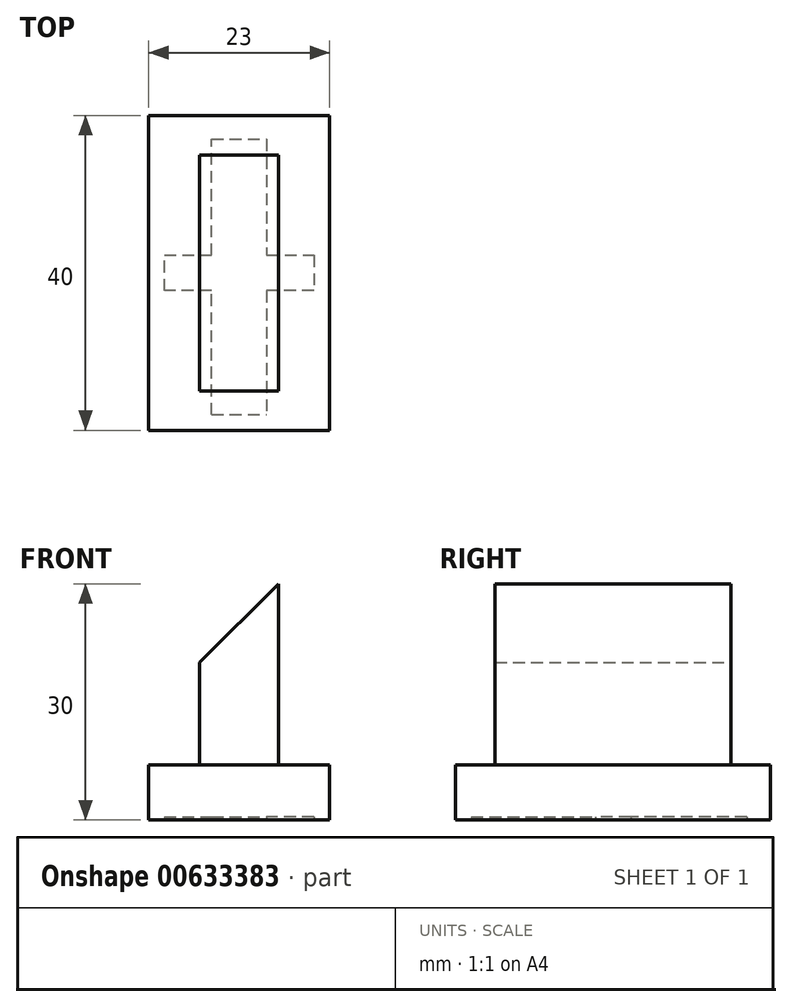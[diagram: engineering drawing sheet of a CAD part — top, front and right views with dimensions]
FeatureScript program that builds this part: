
annotation { "Feature Type Name" : "Feature", "Feature Type Description" : "" }
export const myFeature = defineFeature(function(context is Context, id is Id, definition is map)
    precondition{}
    {
        {
            var Q0;
            Q0=qCreatedBy(makeId("Top.planeOp"),FACE);
            var sketch = newSketch(context, id + "F0", { "sketchPlane" : qUnion([Q0])});
            skLineSegment(sketch, "E0.bottom", {"start": v(0, 0) * mm, "end": v(23, 0) * mm});
            skLineSegment(sketch, "E0.top", {"start": v(0, 40) * mm, "end": v(23, 40) * mm});
            skLineSegment(sketch, "E0.left", {"start": v(0, 0) * mm, "end": v(0, 40) * mm});
            skLineSegment(sketch, "E0.right", {"start": v(23, 0) * mm, "end": v(23, 40) * mm});
            skSolve(sketch);
        }
        {
            var Q0;
            Q0 = qSketchRegion(id + "F0", true);
            extrude(context, id + "F1", {"entities" : qUnion([Q0]), "depth" : 7 * mm, "offsetDistance" : 25 * mm});
        }
        {
            var Q0;
            Q0=qCreatedBy(makeId("Top.planeOp"),FACE);
            var sketch = newSketch(context, id + "F2", { "sketchPlane" : qUnion([Q0])});
            skLineSegment(sketch, "E1.bottom", {"start": v(6.5, 35) * mm, "end": v(16.5, 35) * mm});
            skLineSegment(sketch, "E1.top", {"start": v(6.5, 5) * mm, "end": v(16.5, 5) * mm});
            skLineSegment(sketch, "E1.left", {"start": v(6.5, 35) * mm, "end": v(6.5, 5) * mm});
            skLineSegment(sketch, "E1.right", {"start": v(16.5, 35) * mm, "end": v(16.5, 5) * mm});
            skSolve(sketch);
        }
        {
            var Q0;
            Q0 = qSketchRegion(id + "F2", true);
            extrude(context, id + "F3", {"entities" : qUnion([Q0]), "operationType" : NewBodyOperationType.ADD, "depth" : 30 * mm, "offsetDistance" : 25 * mm});
        }
        {
            var Q0;
            Q0=qCreatedBy(makeId("Top.planeOp"),FACE);
            var sketch = newSketch(context, id + "F4", { "sketchPlane" : qUnion([Q0])});
            skLineSegment(sketch, "E2", {"start": v(8, 2) * mm, "end": v(8, 17.75) * mm});
            skLineSegment(sketch, "E3", {"start": v(8, 17.75) * mm, "end": v(2, 17.75) * mm});
            skLineSegment(sketch, "E4", {"start": v(2, 17.75) * mm, "end": v(2, 22.25) * mm});
            skLineSegment(sketch, "E5", {"start": v(2, 22.25) * mm, "end": v(8, 22.25) * mm});
            skLineSegment(sketch, "E6", {"start": v(8, 22.25) * mm, "end": v(8, 37) * mm});
            skLineSegment(sketch, "E7", {"start": v(8, 37) * mm, "end": v(15, 37) * mm});
            skLineSegment(sketch, "E8", {"start": v(15, 37) * mm, "end": v(15, 22.25) * mm});
            skLineSegment(sketch, "E9", {"start": v(15, 22.25) * mm, "end": v(21, 22.25) * mm});
            skLineSegment(sketch, "E10", {"start": v(21, 22.25) * mm, "end": v(21, 17.75) * mm});
            skLineSegment(sketch, "E11", {"start": v(21, 17.75) * mm, "end": v(15, 17.75) * mm});
            skLineSegment(sketch, "E12", {"start": v(15, 17.75) * mm, "end": v(15, 2) * mm});
            skLineSegment(sketch, "E13", {"start": v(8, 2) * mm, "end": v(15, 2) * mm});
            skSolve(sketch);
        }
        {
            var Q0;
            Q0 = qSketchRegion(id + "F4", true);
            extrude(context, id + "F5", {"entities" : qUnion([Q0]), "operationType" : NewBodyOperationType.REMOVE, "depth" : 0.4 * mm, "offsetDistance" : 25 * mm});
        }
        {
            var Q0;
            Q0=makeQuery(id+"F3.opExtrude","CAP_EDGE",EDGE,{"disambiguationData":[OSD([sQuery(id+"F2.wireOp",EDGE,"E1.left")])],"isStart":false});
            chamfer(context, id + "F6", {"entities" : qUnion([Q0]), "width" : 10 * mm, "tangentPropagation" : true});
        }
    });
